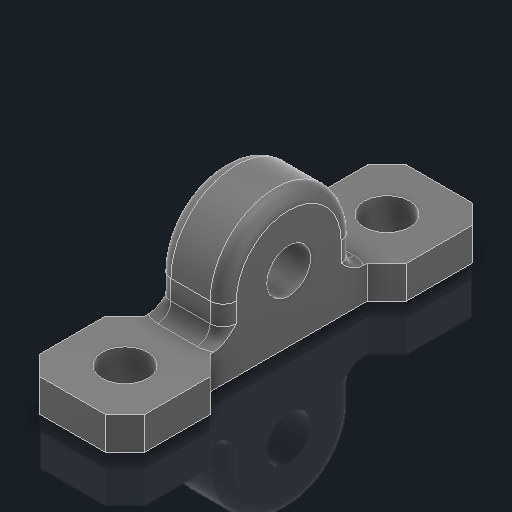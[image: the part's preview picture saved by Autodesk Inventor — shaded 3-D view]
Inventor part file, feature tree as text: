
AUTODESK INVENTOR PART (.ipt)
format: ipt  version: 2023.2 (Build 272271030, 271C)  size: 223,232 bytes
history: native  units: in
note: dims shown in document units (in); Inventor stores cm internally (conversion verified against a paired STEP export)
features: other x3, sketch x3
ambient origin geometry x8: Origin, YZ Plane, XZ Plane, XY Plane, X Axis, Y Axis, Z Axis, Center Point
bodies: Solid1 (feature_tree)
feature tree (6):
  other  "LS Pillow Bearing Block.ipt"
  other  "Solid1::LS Pillow Bearing Block.ipt"
  other  "TaggingFeature1"
  sketch  "Sketch1"  dims[d0=0.3937in]
  sketch  "Sketch2"
  sketch  "Sketch3"
